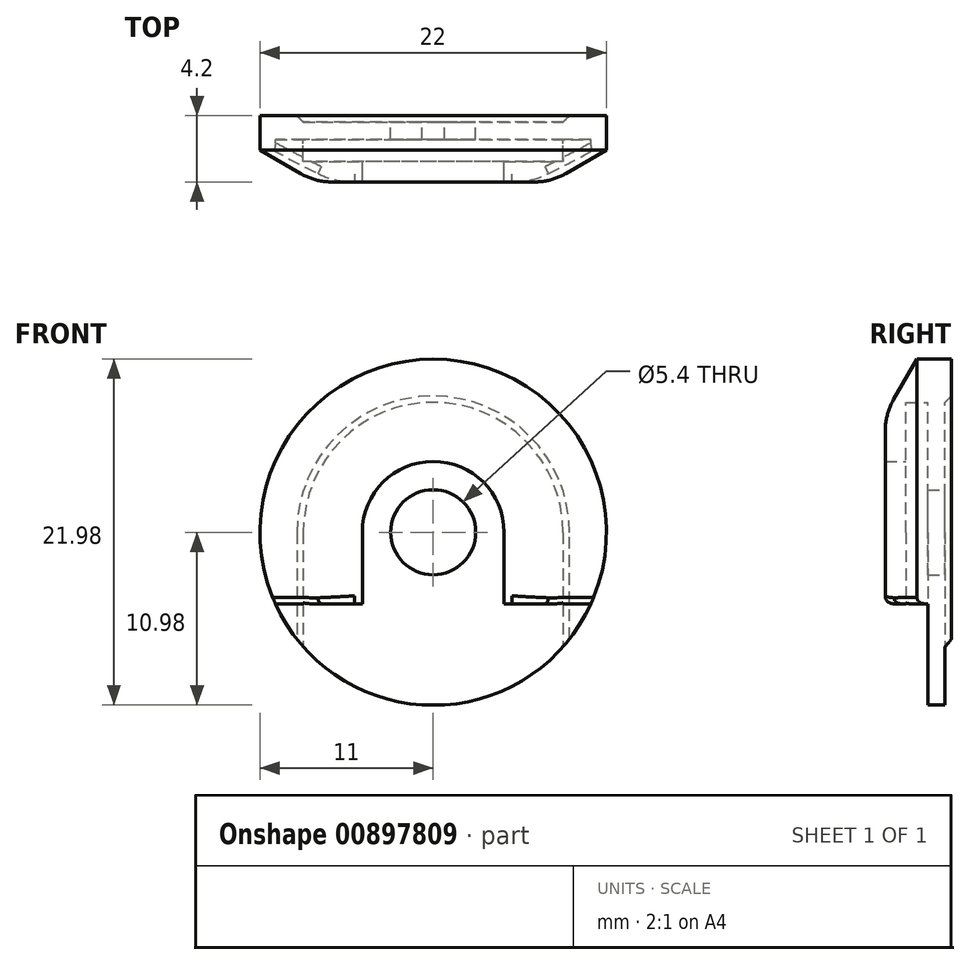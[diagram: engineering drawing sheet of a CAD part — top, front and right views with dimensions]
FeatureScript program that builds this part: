
annotation { "Feature Type Name" : "Feature", "Feature Type Description" : "" }
export const myFeature = defineFeature(function(context is Context, id is Id, definition is map)
    precondition{}
    {
        {
            var Q0;
            Q0=qCreatedBy(makeId("Front.planeOp"),FACE);
            var sketch = newSketch(context, id + "F0", { "sketchPlane" : qUnion([Q0])});
            skCircle(sketch, "E0", {"center": v(0, 0) * mm, "radius": 11 * mm});
            skCircle(sketch, "E1", {"center": v(0, 0) * mm, "radius": 8.25 * mm});
            skCircle(sketch, "E2", {"center": v(0, 0) * mm, "radius": 2.7 * mm});
            skCircle(sketch, "E3", {"center": v(0, 0) * mm, "radius": 4.5 * mm});
            skLineSegment(sketch, "E4", {"start": v(11, 0) * mm, "end": v(11, -10.98) * mm});
            skLineSegment(sketch, "E5", {"start": v(11, -10.98) * mm, "end": v(-10.89, -10.98) * mm});
            skLineSegment(sketch, "E6", {"start": v(-10.89, -10.98) * mm, "end": v(-11, 0) * mm});
            skLineSegment(sketch, "E7", {"start": v(-8.25, 0) * mm, "end": v(-8.25, -10.98) * mm});
            skLineSegment(sketch, "E8", {"start": v(8.25, 0) * mm, "end": v(8.25, -10.98) * mm});
            skLineSegment(sketch, "E9", {"start": v(-4.5, 0) * mm, "end": v(-4.5, -10.98) * mm});
            skLineSegment(sketch, "E10", {"start": v(4.5, 0) * mm, "end": v(4.5, -10.98) * mm});
            skLineSegment(sketch, "E11", {"start": v(-8.25, -4.55) * mm, "end": v(8.25, -4.55) * mm});
            skSolve(sketch);
        }
        {
            var Q0;
            {var subQ7=sQuery(id+"F0.wireOp",EDGE,"E0");var subQ9=makeQuery(id+"F0.imprint","INTERSECT",VERTEX,{"derivedFrom":[subQ7,sQuery(id+"F0.wireOp",EDGE,"E4")]});Q0=makeQuery(id+"F0.imprint","IMPRINT",FACE,{"disambiguationData":[TD([[makeQuery(id+"F0.imprint","IMPRINT",EDGE,{"disambiguationData":[TD([[subQ9,-1.0]])],"derivedFrom":subQ7}),1.0]])]});}
            var Q1;
            {var subQ5=sQuery(id+"F0.wireOp",EDGE,"E1");var subQ6=makeQuery(id+"F0.imprint","INTERSECT",VERTEX,{"derivedFrom":[subQ5,sQuery(id+"F0.wireOp",EDGE,"E7")]});Q1=makeQuery(id+"F0.imprint","IMPRINT",FACE,{"disambiguationData":[TD([[makeQuery(id+"F0.imprint","IMPRINT",EDGE,{"disambiguationData":[TD([[subQ6,1.0]])],"derivedFrom":subQ5}),1.0]])]});}
            var Q2;
            {var subQ0=sQuery(id+"F0.wireOp",EDGE,"E10");var subQ1=sQuery(id+"F0.wireOp",EDGE,"E1");var subQ2=makeQuery(id+"F0.imprint","INTERSECT",VERTEX,{"derivedFrom":[subQ1,subQ0]});Q2=makeQuery(id+"F0.imprint","IMPRINT",FACE,{"disambiguationData":[TD([[makeQuery(id+"F0.imprint","IMPRINT",EDGE,{"disambiguationData":[TD([[subQ2,-1.0]])],"derivedFrom":subQ1}),1.0]])]});}
            var Q3;
            {var subQ0=sQuery(id+"F0.wireOp",EDGE,"E8");var subQ1=sQuery(id+"F0.wireOp",EDGE,"E1");var subQ2=makeQuery(id+"F0.imprint","INTERSECT",VERTEX,{"derivedFrom":[subQ1,subQ0]});Q3=makeQuery(id+"F0.imprint","IMPRINT",FACE,{"disambiguationData":[TD([[makeQuery(id+"F0.imprint","IMPRINT",EDGE,{"disambiguationData":[TD([[subQ2,1.0]])],"derivedFrom":subQ1}),-1.0]])]});}
            var Q4;
            {var subQ0=sQuery(id+"F0.wireOp",EDGE,"E10");var subQ1=sQuery(id+"F0.wireOp",EDGE,"E0");var subQ2=makeQuery(id+"F0.imprint","INTERSECT",VERTEX,{"derivedFrom":[subQ1,subQ0]});Q4=makeQuery(id+"F0.imprint","IMPRINT",FACE,{"disambiguationData":[TD([[makeQuery(id+"F0.imprint","IMPRINT",EDGE,{"disambiguationData":[TD([[subQ2,-1.0]])],"derivedFrom":subQ1}),1.0]])]});}
            var Q5;
            {var subQ0=sQuery(id+"F0.wireOp",EDGE,"E11");var subQ1=sQuery(id+"F0.wireOp",EDGE,"E1");var subQ2=makeQuery(id+"F0.imprint","INTERSECT",VERTEX,{"disambiguationData":[OD(0.0)],"derivedFrom":[subQ1,subQ0]});Q5=makeQuery(id+"F0.imprint","IMPRINT",FACE,{"disambiguationData":[TD([[makeQuery(id+"F0.imprint","IMPRINT",EDGE,{"disambiguationData":[TD([[subQ2,-1.0]])],"derivedFrom":subQ1}),1.0]])]});}
            var Q6;
            {var subQ0=sQuery(id+"F0.wireOp",EDGE,"E7");var subQ1=sQuery(id+"F0.wireOp",EDGE,"E1");var subQ2=makeQuery(id+"F0.imprint","INTERSECT",VERTEX,{"derivedFrom":[subQ1,subQ0]});Q6=makeQuery(id+"F0.imprint","IMPRINT",FACE,{"disambiguationData":[TD([[makeQuery(id+"F0.imprint","IMPRINT",EDGE,{"disambiguationData":[TD([[subQ2,-1.0]])],"derivedFrom":subQ1}),-1.0]])]});}
            var Q7;
            {var subQ1=sQuery(id+"F0.wireOp",EDGE,"E0");var subQ7=sQuery(id+"F0.wireOp",EDGE,"E7");var subQ9=makeQuery(id+"F0.imprint","INTERSECT",VERTEX,{"derivedFrom":[subQ1,subQ7]});Q7=makeQuery(id+"F0.imprint","IMPRINT",FACE,{"disambiguationData":[TD([[makeQuery(id+"F0.imprint","IMPRINT",EDGE,{"disambiguationData":[TD([[subQ9,-1.0]])],"derivedFrom":subQ1}),1.0]])]});}
            extrude(context, id + "F1", {"entities" : qUnion([Q0, Q1, Q2, Q3, Q4, Q5, Q6, Q7]), "depth" : 3.8 * mm, "offsetDistance" : 25 * mm});
        }
        {
            var Q0;
            Q0=makeQuery(id+"F0.imprint","IMPRINT",FACE,{"disambiguationData":[TD([[makeQuery(id+"F0.imprint","IMPRINT",EDGE,{"derivedFrom":sQuery(id+"F0.wireOp",EDGE,"E2")}),-1.0]])]});
            var Q1;
            {var subQ0=sQuery(id+"F0.wireOp",EDGE,"E9");var subQ1=sQuery(id+"F0.wireOp",EDGE,"E3");var subQ2=makeQuery(id+"F0.imprint","INTERSECT",VERTEX,{"derivedFrom":[subQ1,subQ0]});Q1=makeQuery(id+"F0.imprint","IMPRINT",FACE,{"disambiguationData":[TD([[makeQuery(id+"F0.imprint","IMPRINT",EDGE,{"disambiguationData":[TD([[subQ2,-1.0]])],"derivedFrom":subQ1}),-1.0]])]});}
            var Q2;
            {var subQ0=sQuery(id+"F0.wireOp",EDGE,"E9");var subQ1=sQuery(id+"F0.wireOp",EDGE,"E1");var subQ2=makeQuery(id+"F0.imprint","INTERSECT",VERTEX,{"derivedFrom":[subQ1,subQ0]});Q2=makeQuery(id+"F0.imprint","IMPRINT",FACE,{"disambiguationData":[TD([[makeQuery(id+"F0.imprint","IMPRINT",EDGE,{"disambiguationData":[TD([[subQ2,-1.0]])],"derivedFrom":subQ1}),1.0]])]});}
            var Q3;
            {var subQ0=sQuery(id+"F0.wireOp",EDGE,"E5");var subQ1=sQuery(id+"F0.wireOp",EDGE,"E0");var subQ2=makeQuery(id+"F0.imprint","INTERSECT",VERTEX,{"disambiguationData":[OD(0.0)],"derivedFrom":[subQ1,subQ0]});Q3=makeQuery(id+"F0.imprint","IMPRINT",FACE,{"disambiguationData":[TD([[makeQuery(id+"F0.imprint","IMPRINT",EDGE,{"disambiguationData":[TD([[subQ2,1.0]])],"derivedFrom":subQ1}),1.0]])]});}
            extrude(context, id + "F2", {"entities" : qUnion([Q0, Q1, Q2, Q3]), "operationType" : NewBodyOperationType.ADD, "depth" : 1.1 * mm, "offsetDistance" : 25 * mm});
        }
        {
            var Q0;
            {var subQ0=sQuery(id+"F0.wireOp",EDGE,"E7");var subQ1=sQuery(id+"F0.wireOp",EDGE,"E0");var subQ2=makeQuery(id+"F0.imprint","INTERSECT",VERTEX,{"derivedFrom":[subQ1,subQ0]});Q0=makeQuery(id+"F0.imprint","IMPRINT",FACE,{"disambiguationData":[TD([[makeQuery(id+"F0.imprint","IMPRINT",EDGE,{"disambiguationData":[TD([[subQ2,-1.0]])],"derivedFrom":subQ1}),-1.0]])]});}
            var Q1;
            {var subQ1=sQuery(id+"F0.wireOp",EDGE,"E0");var subQ7=sQuery(id+"F0.wireOp",EDGE,"E7");var subQ9=makeQuery(id+"F0.imprint","INTERSECT",VERTEX,{"derivedFrom":[subQ1,subQ7]});Q1=makeQuery(id+"F0.imprint","IMPRINT",FACE,{"disambiguationData":[TD([[makeQuery(id+"F0.imprint","IMPRINT",EDGE,{"disambiguationData":[TD([[subQ9,-1.0]])],"derivedFrom":subQ1}),1.0]])]});}
            var Q2;
            {var subQ0=sQuery(id+"F0.wireOp",EDGE,"E11");var subQ1=sQuery(id+"F0.wireOp",EDGE,"E1");var subQ2=makeQuery(id+"F0.imprint","INTERSECT",VERTEX,{"disambiguationData":[OD(0.0)],"derivedFrom":[subQ1,subQ0]});Q2=makeQuery(id+"F0.imprint","IMPRINT",FACE,{"disambiguationData":[TD([[makeQuery(id+"F0.imprint","IMPRINT",EDGE,{"disambiguationData":[TD([[subQ2,-1.0]])],"derivedFrom":subQ1}),1.0]])]});}
            var Q3;
            {var subQ5=sQuery(id+"F0.wireOp",EDGE,"E1");var subQ6=makeQuery(id+"F0.imprint","INTERSECT",VERTEX,{"derivedFrom":[subQ5,sQuery(id+"F0.wireOp",EDGE,"E7")]});Q3=makeQuery(id+"F0.imprint","IMPRINT",FACE,{"disambiguationData":[TD([[makeQuery(id+"F0.imprint","IMPRINT",EDGE,{"disambiguationData":[TD([[subQ6,1.0]])],"derivedFrom":subQ5}),1.0]])]});}
            var Q4;
            {var subQ0=sQuery(id+"F0.wireOp",EDGE,"E7");var subQ1=sQuery(id+"F0.wireOp",EDGE,"E1");var subQ2=makeQuery(id+"F0.imprint","INTERSECT",VERTEX,{"derivedFrom":[subQ1,subQ0]});Q4=makeQuery(id+"F0.imprint","IMPRINT",FACE,{"disambiguationData":[TD([[makeQuery(id+"F0.imprint","IMPRINT",EDGE,{"disambiguationData":[TD([[subQ2,-1.0]])],"derivedFrom":subQ1}),-1.0]])]});}
            var Q5;
            {var subQ0=sQuery(id+"F0.wireOp",EDGE,"E8");var subQ1=sQuery(id+"F0.wireOp",EDGE,"E1");var subQ2=makeQuery(id+"F0.imprint","INTERSECT",VERTEX,{"derivedFrom":[subQ1,subQ0]});Q5=makeQuery(id+"F0.imprint","IMPRINT",FACE,{"disambiguationData":[TD([[makeQuery(id+"F0.imprint","IMPRINT",EDGE,{"disambiguationData":[TD([[subQ2,1.0]])],"derivedFrom":subQ1}),-1.0]])]});}
            var Q6;
            {var subQ0=sQuery(id+"F0.wireOp",EDGE,"E10");var subQ1=sQuery(id+"F0.wireOp",EDGE,"E0");var subQ2=makeQuery(id+"F0.imprint","INTERSECT",VERTEX,{"derivedFrom":[subQ1,subQ0]});Q6=makeQuery(id+"F0.imprint","IMPRINT",FACE,{"disambiguationData":[TD([[makeQuery(id+"F0.imprint","IMPRINT",EDGE,{"disambiguationData":[TD([[subQ2,-1.0]])],"derivedFrom":subQ1}),1.0]])]});}
            var Q7;
            {var subQ0=sQuery(id+"F0.wireOp",EDGE,"E10");var subQ1=sQuery(id+"F0.wireOp",EDGE,"E1");var subQ2=makeQuery(id+"F0.imprint","INTERSECT",VERTEX,{"derivedFrom":[subQ1,subQ0]});Q7=makeQuery(id+"F0.imprint","IMPRINT",FACE,{"disambiguationData":[TD([[makeQuery(id+"F0.imprint","IMPRINT",EDGE,{"disambiguationData":[TD([[subQ2,-1.0]])],"derivedFrom":subQ1}),1.0]])]});}
            var Q8;
            {var subQ0=sQuery(id+"F0.wireOp",EDGE,"E10");var subQ1=sQuery(id+"F0.wireOp",EDGE,"E0");var subQ2=makeQuery(id+"F0.imprint","INTERSECT",VERTEX,{"derivedFrom":[subQ1,subQ0]});Q8=makeQuery(id+"F0.imprint","IMPRINT",FACE,{"disambiguationData":[TD([[makeQuery(id+"F0.imprint","IMPRINT",EDGE,{"disambiguationData":[TD([[subQ2,-1.0]])],"derivedFrom":subQ1}),-1.0]])]});}
            extrude(context, id + "F3", {"entities" : qUnion([Q0, Q1, Q2, Q3, Q4, Q5, Q6, Q7, Q8]), "operationType" : NewBodyOperationType.REMOVE, "endBound" : BoundingType.UP_TO_NEXT, "depth" : 1.3 * mm, "hasOffset" : true, "offsetDistance" : 1.3 * mm, "hasSecondDirection" : true, "secondDirectionOppositeDirection" : false, "secondDirectionDepth" : 1.1 * mm});
        }
        {
            var Q0;
            Q0=makeQuery(id+"F1.opExtrude","CAP_EDGE",EDGE,{"disambiguationData":[OSD([sQuery(id+"F0.wireOp",EDGE,"E6")])],"isStart":false});
            var Q1;
            Q1=makeQuery(id+"F1.opExtrude","CAP_EDGE",EDGE,{"disambiguationData":[OSD([sQuery(id+"F0.wireOp",EDGE,"E0")])],"isStart":false});
            var Q2;
            Q2=makeQuery(id+"F1.opExtrude","CAP_EDGE",EDGE,{"disambiguationData":[OSD([sQuery(id+"F0.wireOp",EDGE,"E4")])],"isStart":false});
            chamfer(context, id + "F4", {"entities" : qUnion([Q0, Q1, Q2]), "chamferType" : ChamferType.OFFSET_ANGLE, "width" : 3.5 * mm, "oppositeDirection" : false, "angle" : 30 * degree, "tangentPropagation" : true});
        }
        {
            var Q0;
            {var subQ0=sQuery(id+"F0.wireOp",EDGE,"E0");Q0=makeQuery(id+"F4.opChamfer","BLEND_EDGE",EDGE,{"blendedFrom":[makeQuery(id+"F1.opExtrude","CAP_EDGE",EDGE,{"disambiguationData":[OSD([subQ0])],"isStart":false}),makeQuery(id+"F1.opExtrude","CAP_FACE",FACE,{"disambiguationData":[OSD([subQ0,sQuery(id+"F0.wireOp",EDGE,"E3"),sQuery(id+"F0.wireOp",EDGE,"E4"),sQuery(id+"F0.wireOp",EDGE,"E5"),sQuery(id+"F0.wireOp",EDGE,"E6"),sQuery(id+"F0.wireOp",EDGE,"E9"),sQuery(id+"F0.wireOp",EDGE,"E10")])],"isStart":false})],"blendedInto":[makeQuery(id+"F1.opExtrude","CAP_FACE",FACE,{"disambiguationData":[OSD([subQ0,sQuery(id+"F0.wireOp",EDGE,"E3"),sQuery(id+"F0.wireOp",EDGE,"E4"),sQuery(id+"F0.wireOp",EDGE,"E5"),sQuery(id+"F0.wireOp",EDGE,"E6"),sQuery(id+"F0.wireOp",EDGE,"E9"),sQuery(id+"F0.wireOp",EDGE,"E10")])],"isStart":false})]});}
            var Q1;
            {var subQ0=sQuery(id+"F0.wireOp",EDGE,"E6");Q1=makeQuery(id+"F4.opChamfer","BLEND_EDGE",EDGE,{"blendedFrom":[makeQuery(id+"F1.opExtrude","CAP_EDGE",EDGE,{"disambiguationData":[OSD([subQ0])],"isStart":false}),makeQuery(id+"F1.opExtrude","CAP_FACE",FACE,{"disambiguationData":[OSD([sQuery(id+"F0.wireOp",EDGE,"E0"),sQuery(id+"F0.wireOp",EDGE,"E3"),sQuery(id+"F0.wireOp",EDGE,"E4"),sQuery(id+"F0.wireOp",EDGE,"E5"),subQ0,sQuery(id+"F0.wireOp",EDGE,"E9"),sQuery(id+"F0.wireOp",EDGE,"E10")])],"isStart":false})],"blendedInto":[makeQuery(id+"F1.opExtrude","CAP_FACE",FACE,{"disambiguationData":[OSD([sQuery(id+"F0.wireOp",EDGE,"E0"),sQuery(id+"F0.wireOp",EDGE,"E3"),sQuery(id+"F0.wireOp",EDGE,"E4"),sQuery(id+"F0.wireOp",EDGE,"E5"),subQ0,sQuery(id+"F0.wireOp",EDGE,"E9"),sQuery(id+"F0.wireOp",EDGE,"E10")])],"isStart":false})]});}
            var Q2;
            {var subQ0=sQuery(id+"F0.wireOp",EDGE,"E4");Q2=makeQuery(id+"F4.opChamfer","BLEND_EDGE",EDGE,{"blendedFrom":[makeQuery(id+"F1.opExtrude","CAP_EDGE",EDGE,{"disambiguationData":[OSD([subQ0])],"isStart":false}),makeQuery(id+"F1.opExtrude","CAP_FACE",FACE,{"disambiguationData":[OSD([sQuery(id+"F0.wireOp",EDGE,"E0"),sQuery(id+"F0.wireOp",EDGE,"E3"),subQ0,sQuery(id+"F0.wireOp",EDGE,"E5"),sQuery(id+"F0.wireOp",EDGE,"E6"),sQuery(id+"F0.wireOp",EDGE,"E9"),sQuery(id+"F0.wireOp",EDGE,"E10")])],"isStart":false})],"blendedInto":[makeQuery(id+"F1.opExtrude","CAP_FACE",FACE,{"disambiguationData":[OSD([sQuery(id+"F0.wireOp",EDGE,"E0"),sQuery(id+"F0.wireOp",EDGE,"E3"),subQ0,sQuery(id+"F0.wireOp",EDGE,"E5"),sQuery(id+"F0.wireOp",EDGE,"E6"),sQuery(id+"F0.wireOp",EDGE,"E9"),sQuery(id+"F0.wireOp",EDGE,"E10")])],"isStart":false})]});}
            fillet(context, id + "F5", {"entities" : qUnion([Q0, Q1, Q2]), "radius" : 4 * mm, "tangentPropagation" : true, "allowEdgeOverflow" : false});
        }
        {
            var Q0;
            Q0=qCreatedBy(makeId("Right.planeOp"),FACE);
            var sketch = newSketch(context, id + "F6", { "sketchPlane" : qUnion([Q0])});
            skLineSegment(sketch, "E12", {"start": v(0, -4.54) * mm, "end": v(-1.1, -4.54) * mm});
            skLineSegment(sketch, "E13", {"start": v(0, -10.98) * mm, "end": v(-1.1, -10.98) * mm});
            skLineSegment(sketch, "E14", {"start": v(-1.1, -4.54) * mm, "end": v(-3.8, -4.54) * mm});
            skLineSegment(sketch, "E15", {"start": v(-3.8, -4.54) * mm, "end": v(-3.8, -10.97) * mm});
            skLineSegment(sketch, "E16", {"start": v(-3.8, -10.97) * mm, "end": v(-1.1, -10.98) * mm});
            skLineSegment(sketch, "E17", {"start": v(-1.1, -10.98) * mm, "end": v(-1.1, -4.54) * mm});
            skSolve(sketch);
        }
        {
            var Q0;
            Q0=makeQuery(id+"F6.imprint","IMPRINT",FACE,{"disambiguationData":[TD([[makeQuery(id+"F6.imprint","IMPRINT",EDGE,{"derivedFrom":sQuery(id+"F6.wireOp",EDGE,"E14")}),1.0]])]});
            extrude(context, id + "F7", {"entities" : qUnion([Q0]), "operationType" : NewBodyOperationType.REMOVE, "depth" : 25 * mm, "offsetDistance" : 25 * mm, "hasSecondDirection" : true, "secondDirectionOppositeDirection" : true, "secondDirectionDepth" : 25 * mm});
        }
        {
            var Q0;
            Q0=makeQuery(id+"F7.boolean.opBoolean","INTERSECT",EDGE,{"disambiguationData":[OD(1.0)],"derivedFrom":[makeQuery(id+"F1.opExtrude","CAP_FACE",FACE,{"disambiguationData":[OSD([sQuery(id+"F0.wireOp",EDGE,"E0"),sQuery(id+"F0.wireOp",EDGE,"E3"),sQuery(id+"F0.wireOp",EDGE,"E4"),sQuery(id+"F0.wireOp",EDGE,"E5"),sQuery(id+"F0.wireOp",EDGE,"E6"),sQuery(id+"F0.wireOp",EDGE,"E9"),sQuery(id+"F0.wireOp",EDGE,"E10")])],"isStart":false}),makeQuery(id+"F7.opExtrude","SWEPT_FACE",FACE,{"disambiguationData":[OSD([sQuery(id+"F6.wireOp",EDGE,"E14")])]})]});
            var Q1;
            Q1=makeQuery(id+"F7.boolean.opBoolean","INTERSECT",EDGE,{"disambiguationData":[OD(0.0)],"derivedFrom":[makeQuery(id+"F1.opExtrude","CAP_FACE",FACE,{"disambiguationData":[OSD([sQuery(id+"F0.wireOp",EDGE,"E0"),sQuery(id+"F0.wireOp",EDGE,"E3"),sQuery(id+"F0.wireOp",EDGE,"E4"),sQuery(id+"F0.wireOp",EDGE,"E5"),sQuery(id+"F0.wireOp",EDGE,"E6"),sQuery(id+"F0.wireOp",EDGE,"E9"),sQuery(id+"F0.wireOp",EDGE,"E10")])],"isStart":false}),makeQuery(id+"F7.opExtrude","SWEPT_FACE",FACE,{"disambiguationData":[OSD([sQuery(id+"F6.wireOp",EDGE,"E14")])]})]});
            var Q2;
            Q2=makeQuery(id+"F7.boolean.opBoolean","INTERSECT",EDGE,{"derivedFrom":[makeQuery(id+"F4.opChamfer","BLEND_FACE",FACE,{"disambiguationData":[OSD([sQuery(id+"F0.wireOp",EDGE,"E6")])]}),makeQuery(id+"F7.opExtrude","SWEPT_FACE",FACE,{"disambiguationData":[OSD([sQuery(id+"F6.wireOp",EDGE,"E17")])]})]});
            var Q3;
            Q3=makeQuery(id+"F7.boolean.opBoolean","INTERSECT",EDGE,{"derivedFrom":[makeQuery(id+"F4.opChamfer","BLEND_FACE",FACE,{"disambiguationData":[OSD([sQuery(id+"F0.wireOp",EDGE,"E4")])]}),makeQuery(id+"F7.opExtrude","SWEPT_FACE",FACE,{"disambiguationData":[OSD([sQuery(id+"F6.wireOp",EDGE,"E17")])]})]});
            fillet(context, id + "F8", {"entities" : qUnion([Q0, Q1, Q2, Q3]), "radius" : 0.5 * mm, "tangentPropagation" : true, "allowEdgeOverflow" : false});
        }
        {
            var Q0;
            {var subQ7=sQuery(id+"F0.wireOp",EDGE,"E0");var subQ9=makeQuery(id+"F0.imprint","INTERSECT",VERTEX,{"derivedFrom":[subQ7,sQuery(id+"F0.wireOp",EDGE,"E4")]});Q0=makeQuery(id+"F0.imprint","IMPRINT",FACE,{"disambiguationData":[TD([[makeQuery(id+"F0.imprint","IMPRINT",EDGE,{"disambiguationData":[TD([[subQ9,-1.0]])],"derivedFrom":subQ7}),1.0]])]});}
            extrude(context, id + "F9", {"entities" : qUnion([Q0]), "operationType" : NewBodyOperationType.ADD, "oppositeDirection" : true, "depth" : 0.4 * mm, "offsetDistance" : 25 * mm});
        }
        {
            var Q0;
            Q0=makeQuery(id+"F9.opExtrude","CAP_EDGE",EDGE,{"disambiguationData":[OSD([sQuery(id+"F0.wireOp",EDGE,"E1")])],"isStart":false});
            chamfer(context, id + "F10", {"entities" : qUnion([Q0]), "width" : 0.4 * mm, "tangentPropagation" : true});
        }
    });
